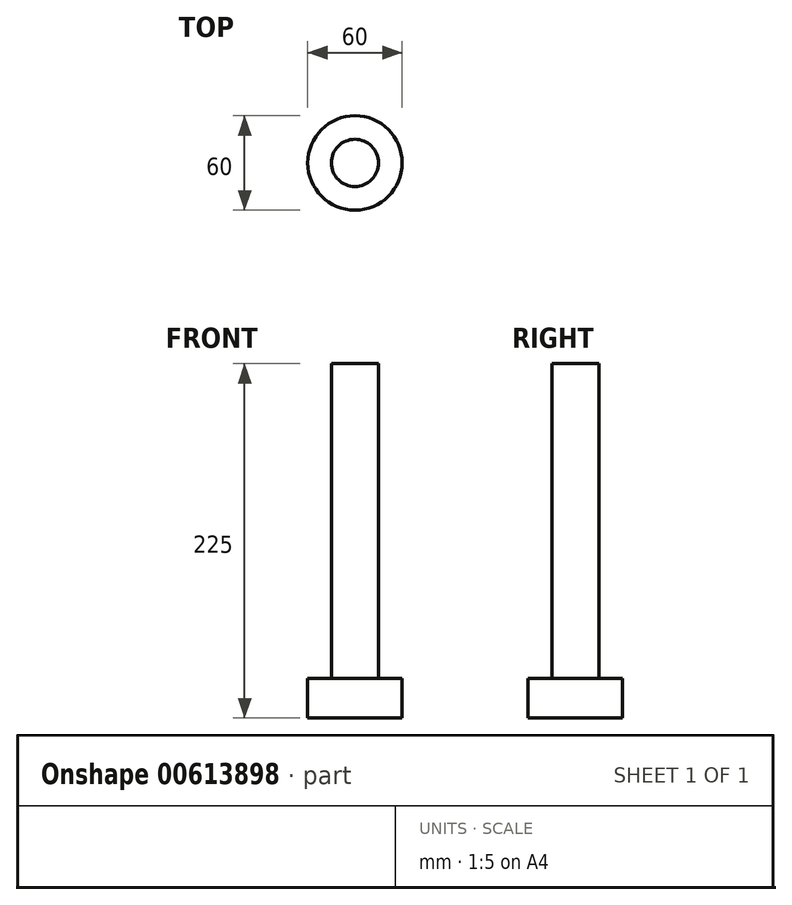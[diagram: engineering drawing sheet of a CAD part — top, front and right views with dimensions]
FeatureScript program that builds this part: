
annotation { "Feature Type Name" : "Feature", "Feature Type Description" : "" }
export const myFeature = defineFeature(function(context is Context, id is Id, definition is map)
    precondition{}
    {
        {
            var Q0;
            Q0=qCreatedBy(makeId("Top.planeOp"),FACE);
            var sketch = newSketch(context, id + "F0", { "sketchPlane" : qUnion([Q0])});
            skCircle(sketch, "E0", {"center": v(0, 0) * mm, "radius": 15 * mm});
            skSolve(sketch);
        }
        {
            var Q0;
            Q0 = qSketchRegion(id + "F0", true);
            extrude(context, id + "F1", {"entities" : qUnion([Q0]), "depth" : 225 * mm, "offsetDistance" : 25 * mm});
        }
        {
            var Q0;
            Q0=qCreatedBy(makeId("Top.planeOp"),FACE);
            var sketch = newSketch(context, id + "F2", { "sketchPlane" : qUnion([Q0])});
            skCircle(sketch, "E1", {"center": v(0, 0) * mm, "radius": 30 * mm});
            skSolve(sketch);
        }
        {
            var Q0;
            Q0 = qSketchRegion(id + "F2", true);
            extrude(context, id + "F3", {"entities" : qUnion([Q0]), "operationType" : NewBodyOperationType.ADD, "depth" : 25 * mm, "offsetDistance" : 25 * mm});
        }
    });
